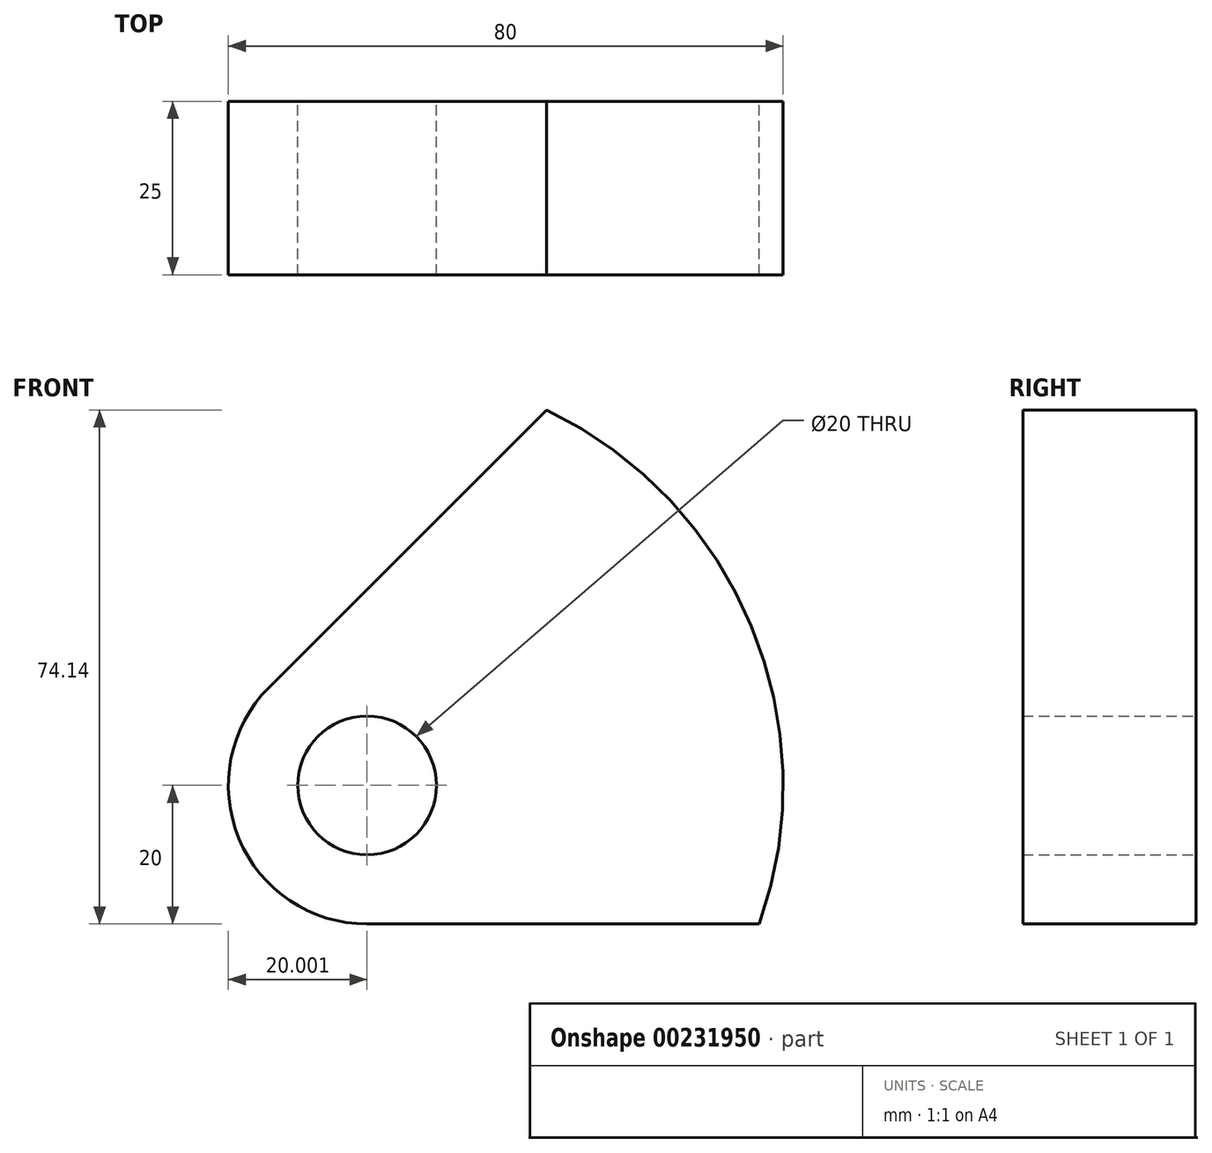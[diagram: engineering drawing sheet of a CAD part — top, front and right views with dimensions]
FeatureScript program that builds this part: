
annotation { "Feature Type Name" : "Feature", "Feature Type Description" : "" }
export const myFeature = defineFeature(function(context is Context, id is Id, definition is map)
    precondition{}
    {
        {
            var Q0;
            Q0=qCreatedBy(makeId("Front.planeOp"),FACE);
            var sketch = newSketch(context, id + "F0", { "sketchPlane" : qUnion([Q0])});
            skLineSegment(sketch, "E0", {"start": v(0, 0) * mm, "end": v(-56.57, 0) * mm});
            skArc(sketch, "E1", {"start": v(-56.57, 0) * mm, "mid": v(-75.05, 12.35) * mm, "end": v(-70.71, 34.14) * mm});
            skLineSegment(sketch, "E2", {"start": v(-70.71, 34.14) * mm, "end": v(-30.71, 74.14) * mm});
            skCircle(sketch, "E3", {"center": v(-56.57, 20) * mm, "radius": 10 * mm});
            skArc(sketch, "E4", {"start": v(0, 0) * mm, "mid": v(-1.14, 42.96) * mm, "end": v(-30.71, 74.14) * mm});
            skSolve(sketch);
        }
        {
            var Q0;
            Q0=makeQuery(id+"F0.imprint","IMPRINT",FACE,{"disambiguationData":[TD([[makeQuery(id+"F0.imprint","IMPRINT",EDGE,{"derivedFrom":sQuery(id+"F0.wireOp",EDGE,"E0")}),-1.0]])]});
            extrude(context, id + "F1", {"entities" : qUnion([Q0]), "depth" : 25 * mm});
        }
    });
